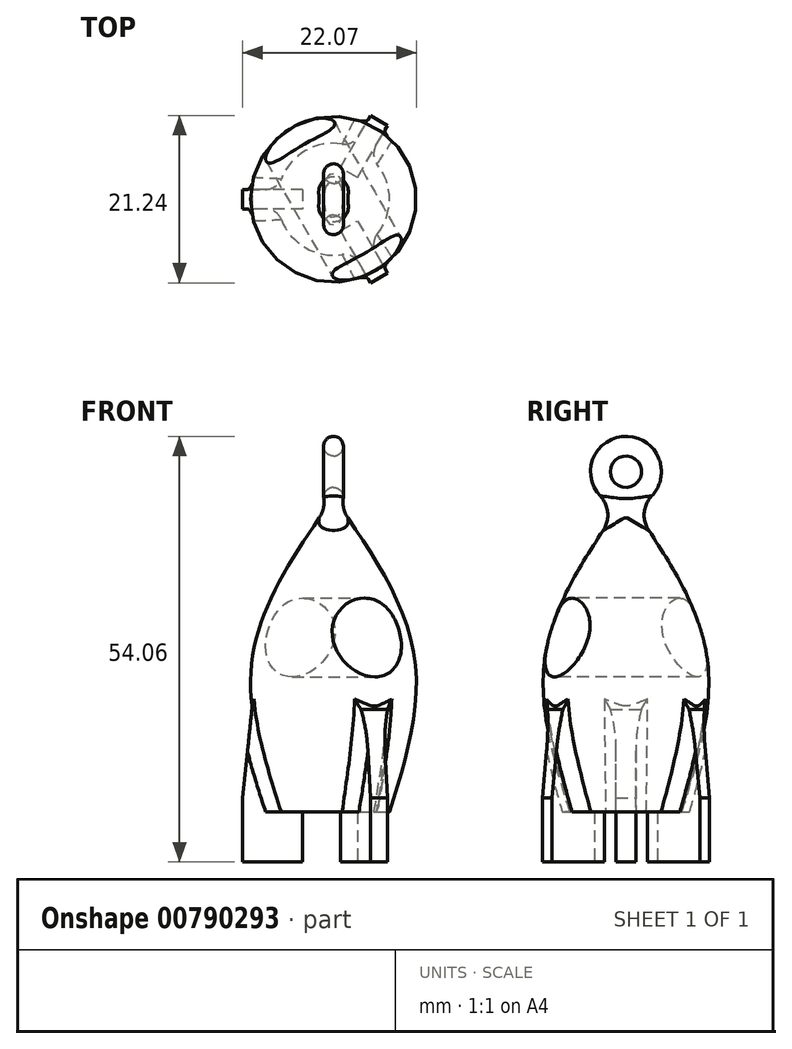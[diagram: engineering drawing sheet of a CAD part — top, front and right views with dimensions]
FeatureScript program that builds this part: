
annotation { "Feature Type Name" : "Feature", "Feature Type Description" : "" }
export const myFeature = defineFeature(function(context is Context, id is Id, definition is map)
    precondition{}
    {
        {
            var Q0;
            Q0=qCreatedBy(makeId("Front.planeOp"),FACE);
            var sketch = newSketch(context, id + "F0", { "sketchPlane" : qUnion([Q0])});
            skLineSegment(sketch, "E0", {"start": v(0, 20) * mm, "end": v(0, -20) * mm});
            skFitSpline(sketch, "E1", {"points": [v(0, 20) * mm, v(-10.25, 0) * mm, v(-7.11, -20) * mm], "startDerivative": vector(-26.7, -38.64) * mm, "endDerivative": vector(12.86, -41.38) * mm});
            skLineSegment(sketch, "E2", {"start": v(-7.11, -20) * mm, "end": v(0, -20) * mm});
            skSolve(sketch);
        }
        {
            var Q0;
            Q0=makeQuery(id+"F0.imprint","IMPRINT",FACE,{"disambiguationData":[TD([[makeQuery(id+"F0.imprint","IMPRINT",EDGE,{"derivedFrom":sQuery(id+"F0.wireOp",EDGE,"E0")}),-1.0]])]});
            var Q1;
            Q1=sQuery(id+"F0.wireOp",EDGE,"E0");
            revolve(context, id + "F1", {"surfaceOperationType" : NewSurfaceOperationType.NEW, "entities" : qUnion([Q0]), "axis" : qUnion([Q1]), "revolveType" : RevolveType.FULL});
        }
        {
            var Q0;
            Q0=qCreatedBy(makeId("Front.planeOp"),FACE);
            var sketch = newSketch(context, id + "F2", { "sketchPlane" : qUnion([Q0])});
            skLineSegment(sketch, "E3", {"start": v(-3.9, -6.95) * mm, "end": v(-3.9, -26.33) * mm});
            skLineSegment(sketch, "E4", {"start": v(-3.9, -26.33) * mm, "end": v(-11.54, -26.33) * mm});
            skLineSegment(sketch, "E5", {"start": v(-11.54, -26.33) * mm, "end": v(-11.54, -18.2) * mm});
            skLineSegment(sketch, "E6", {"start": v(-11.54, -18.2) * mm, "end": v(-10.37, -6.95) * mm});
            skLineSegment(sketch, "E7", {"start": v(-10.37, -6.95) * mm, "end": v(-3.9, -6.95) * mm});
            skSolve(sketch);
        }
        {
            var Q0;
            Q0 = qSketchRegion(id + "F2", true);
            extrude(context, id + "F3", {"entities" : qUnion([Q0]), "depth" : 2.5 * mm, "offsetDistance" : 25 * mm, "symmetric" : true});
        }
        {
            var Q0;
            Q0=makeQuery(id+"F3.opExtrude","SWEPT_BODY",BODY,{"disambiguationData":[OSD([sQuery(id+"F2.wireOp",EDGE,"E3"),sQuery(id+"F2.wireOp",EDGE,"E4"),sQuery(id+"F2.wireOp",EDGE,"E5"),sQuery(id+"F2.wireOp",EDGE,"E6"),sQuery(id+"F2.wireOp",EDGE,"E7")])]});
            var Q1;
            Q1=sQuery(id+"F0.wireOp",EDGE,"E0");
            circularPattern(context, id + "F4", {"entities" : qUnion([Q0]), "axis" : qUnion([Q1]), "angle" : 360 * degree, "instanceCount" : 3, "equalSpace" : true});
        }
        {
            var Q0;
            Q0=makeQuery(id+"F4.opPattern","COPY",FACE,{"derivedFrom":makeQuery(id+"F3.opExtrude","SWEPT_FACE",FACE,{"disambiguationData":[OSD([sQuery(id+"F2.wireOp",EDGE,"E5")])]}),"instanceName":"2"});
            var sketch = newSketch(context, id + "F5", { "sketchPlane" : qUnion([Q0])});
            skCircle(sketch, "E8", {"center": v(0, 2.17) * mm, "radius": 5 * mm});
            skSolve(sketch);
        }
        {
            var Q0;
            Q0=makeQuery(id+"F5.imprint","IMPRINT",FACE,{"disambiguationData":[TD([[makeQuery(id+"F5.imprint","IMPRINT",EDGE,{"derivedFrom":sQuery(id+"F5.wireOp",EDGE,"E8")}),1.0]])]});
            extrude(context, id + "F6", {"entities" : qUnion([Q0]), "operationType" : NewBodyOperationType.REMOVE, "endBound" : BoundingType.THROUGH_ALL, "oppositeDirection" : true, "depth" : 25 * mm, "offsetDistance" : 25 * mm});
        }
        {
            var Q0;
            Q0=qCreatedBy(makeId("Front.planeOp"),FACE);
            var sketch = newSketch(context, id + "F7", { "sketchPlane" : qUnion([Q0])});
            skCircle(sketch, "E9", {"center": v(0, 19.98) * mm, "radius": 1.25 * mm});
            skLineSegment(sketch, "E10", {"start": v(-4.69, 23.23) * mm, "end": v(7.72, 23.23) * mm});
            skSolve(sketch);
        }
        {
            var Q0;
            Q0 = qSketchRegion(id + "F7", true);
            var Q1;
            Q1=sQuery(id+"F7.wireOp",EDGE,"E10");
            revolve(context, id + "F8", {"surfaceOperationType" : NewSurfaceOperationType.NEW, "entities" : qUnion([Q0]), "axis" : qUnion([Q1]), "revolveType" : RevolveType.FULL});
        }
        {
            var Q0;
            Q0=makeQuery(id+"F1.opRevolve","SWEPT_BODY",BODY,{"disambiguationData":[OSD([sQuery(id+"F0.wireOp",EDGE,"E0"),sQuery(id+"F0.wireOp",EDGE,"E1"),sQuery(id+"F0.wireOp",EDGE,"E2")])]});
            var Q1;
            Q1=makeQuery(id+"F3.opExtrude","SWEPT_BODY",BODY,{"disambiguationData":[OSD([sQuery(id+"F2.wireOp",EDGE,"E3"),sQuery(id+"F2.wireOp",EDGE,"E4"),sQuery(id+"F2.wireOp",EDGE,"E5"),sQuery(id+"F2.wireOp",EDGE,"E6"),sQuery(id+"F2.wireOp",EDGE,"E7")])]});
            var Q2;
            Q2=makeQuery(id+"F4.opPattern","COPY",BODY,{"derivedFrom":makeQuery(id+"F3.opExtrude","SWEPT_BODY",BODY,{"disambiguationData":[OSD([sQuery(id+"F2.wireOp",EDGE,"E3"),sQuery(id+"F2.wireOp",EDGE,"E4"),sQuery(id+"F2.wireOp",EDGE,"E5"),sQuery(id+"F2.wireOp",EDGE,"E6"),sQuery(id+"F2.wireOp",EDGE,"E7")])]}),"instanceName":"1"});
            var Q3;
            Q3=makeQuery(id+"F4.opPattern","COPY",BODY,{"derivedFrom":makeQuery(id+"F3.opExtrude","SWEPT_BODY",BODY,{"disambiguationData":[OSD([sQuery(id+"F2.wireOp",EDGE,"E3"),sQuery(id+"F2.wireOp",EDGE,"E4"),sQuery(id+"F2.wireOp",EDGE,"E5"),sQuery(id+"F2.wireOp",EDGE,"E6"),sQuery(id+"F2.wireOp",EDGE,"E7")])]}),"instanceName":"2"});
            var Q4;
            Q4=makeQuery(id+"F8.opRevolve","SWEPT_BODY",BODY,{"disambiguationData":[OSD([sQuery(id+"F7.wireOp",EDGE,"E9")])]});
            booleanBodies(context, id + "F9", {"operationType" : BooleanOperationType.UNION, "tools" : qUnion([Q0, Q1, Q2, Q3, Q4])});
        }
        {
            var Q0;
            Q0=makeQuery(id+"F9.opBoolean","INTERSECT",EDGE,{"derivedFrom":[makeQuery(id+"F1.opRevolve","SWEPT_FACE",FACE,{"disambiguationData":[OSD([sQuery(id+"F0.wireOp",EDGE,"E1")])]}),makeQuery(id+"F8.opRevolve","SWEPT_FACE",FACE,{"disambiguationData":[OSD([sQuery(id+"F7.wireOp",EDGE,"E9")])]})]});
            fillet(context, id + "F10", {"entities" : qUnion([Q0]), "radius" : 3.5 * mm, "tangentPropagation" : true, "allowEdgeOverflow" : false});
        }
        {
            var Q0;
            Q0=makeQuery(id+"F9.opBoolean","INTERSECT",EDGE,{"derivedFrom":[makeQuery(id+"F4.opPattern","COPY",FACE,{"derivedFrom":makeQuery(id+"F3.opExtrude","CAP_FACE",FACE,{"disambiguationData":[OSD([sQuery(id+"F2.wireOp",EDGE,"E3"),sQuery(id+"F2.wireOp",EDGE,"E4"),sQuery(id+"F2.wireOp",EDGE,"E5"),sQuery(id+"F2.wireOp",EDGE,"E6"),sQuery(id+"F2.wireOp",EDGE,"E7")])],"isStart":false}),"instanceName":"1"}),makeQuery(id+"F1.opRevolve","SWEPT_FACE",FACE,{"disambiguationData":[OSD([sQuery(id+"F0.wireOp",EDGE,"E1")])]})]});
            var Q1;
            Q1=makeQuery(id+"F9.opBoolean","INTERSECT",EDGE,{"derivedFrom":[makeQuery(id+"F4.opPattern","COPY",FACE,{"derivedFrom":makeQuery(id+"F3.opExtrude","CAP_FACE",FACE,{"disambiguationData":[OSD([sQuery(id+"F2.wireOp",EDGE,"E3"),sQuery(id+"F2.wireOp",EDGE,"E4"),sQuery(id+"F2.wireOp",EDGE,"E5"),sQuery(id+"F2.wireOp",EDGE,"E6"),sQuery(id+"F2.wireOp",EDGE,"E7")])],"isStart":true}),"instanceName":"1"}),makeQuery(id+"F1.opRevolve","SWEPT_FACE",FACE,{"disambiguationData":[OSD([sQuery(id+"F0.wireOp",EDGE,"E1")])]})]});
            fillet(context, id + "F11", {"entities" : qUnion([Q0, Q1]), "radius" : 2 * mm, "tangentPropagation" : true, "allowEdgeOverflow" : false});
        }
        {
            var Q0;
            Q0=makeQuery(id+"F9.opBoolean","INTERSECT",EDGE,{"derivedFrom":[makeQuery(id+"F4.opPattern","COPY",FACE,{"derivedFrom":makeQuery(id+"F3.opExtrude","CAP_FACE",FACE,{"disambiguationData":[OSD([sQuery(id+"F2.wireOp",EDGE,"E3"),sQuery(id+"F2.wireOp",EDGE,"E4"),sQuery(id+"F2.wireOp",EDGE,"E5"),sQuery(id+"F2.wireOp",EDGE,"E6"),sQuery(id+"F2.wireOp",EDGE,"E7")])],"isStart":false}),"instanceName":"2"}),makeQuery(id+"F1.opRevolve","SWEPT_FACE",FACE,{"disambiguationData":[OSD([sQuery(id+"F0.wireOp",EDGE,"E1")])]})]});
            var Q1;
            Q1=makeQuery(id+"F9.opBoolean","INTERSECT",EDGE,{"derivedFrom":[makeQuery(id+"F4.opPattern","COPY",FACE,{"derivedFrom":makeQuery(id+"F3.opExtrude","CAP_FACE",FACE,{"disambiguationData":[OSD([sQuery(id+"F2.wireOp",EDGE,"E3"),sQuery(id+"F2.wireOp",EDGE,"E4"),sQuery(id+"F2.wireOp",EDGE,"E5"),sQuery(id+"F2.wireOp",EDGE,"E6"),sQuery(id+"F2.wireOp",EDGE,"E7")])],"isStart":true}),"instanceName":"2"}),makeQuery(id+"F1.opRevolve","SWEPT_FACE",FACE,{"disambiguationData":[OSD([sQuery(id+"F0.wireOp",EDGE,"E1")])]})]});
            fillet(context, id + "F12", {"entities" : qUnion([Q0, Q1]), "radius" : 2 * mm, "tangentPropagation" : true, "allowEdgeOverflow" : false});
        }
        {
            var Q0;
            Q0=makeQuery(id+"F9.opBoolean","INTERSECT",EDGE,{"derivedFrom":[makeQuery(id+"F3.opExtrude","CAP_FACE",FACE,{"disambiguationData":[OSD([sQuery(id+"F2.wireOp",EDGE,"E3"),sQuery(id+"F2.wireOp",EDGE,"E4"),sQuery(id+"F2.wireOp",EDGE,"E5"),sQuery(id+"F2.wireOp",EDGE,"E6"),sQuery(id+"F2.wireOp",EDGE,"E7")])],"isStart":true}),makeQuery(id+"F1.opRevolve","SWEPT_FACE",FACE,{"disambiguationData":[OSD([sQuery(id+"F0.wireOp",EDGE,"E1")])]})]});
            var Q1;
            Q1=makeQuery(id+"F9.opBoolean","INTERSECT",EDGE,{"derivedFrom":[makeQuery(id+"F3.opExtrude","CAP_FACE",FACE,{"disambiguationData":[OSD([sQuery(id+"F2.wireOp",EDGE,"E3"),sQuery(id+"F2.wireOp",EDGE,"E4"),sQuery(id+"F2.wireOp",EDGE,"E5"),sQuery(id+"F2.wireOp",EDGE,"E6"),sQuery(id+"F2.wireOp",EDGE,"E7")])],"isStart":false}),makeQuery(id+"F1.opRevolve","SWEPT_FACE",FACE,{"disambiguationData":[OSD([sQuery(id+"F0.wireOp",EDGE,"E1")])]})]});
            fillet(context, id + "F13", {"entities" : qUnion([Q0, Q1]), "radius" : 2 * mm, "tangentPropagation" : true, "allowEdgeOverflow" : false});
        }
        {
            var Q0;
            Q0=makeQuery(id+"F9.opBoolean","INTERSECT",EDGE,{"derivedFrom":[makeQuery(id+"F4.opPattern","COPY",FACE,{"derivedFrom":makeQuery(id+"F3.opExtrude","SWEPT_FACE",FACE,{"disambiguationData":[OSD([sQuery(id+"F2.wireOp",EDGE,"E7")])]}),"instanceName":"2"}),makeQuery(id+"F1.opRevolve","SWEPT_FACE",FACE,{"disambiguationData":[OSD([sQuery(id+"F0.wireOp",EDGE,"E1")])]})]});
            fillet(context, id + "F14", {"entities" : qUnion([Q0]), "radius" : 2 * mm, "tangentPropagation" : true, "allowEdgeOverflow" : false});
        }
        {
            var Q0;
            Q0=makeQuery(id+"F9.opBoolean","INTERSECT",EDGE,{"derivedFrom":[makeQuery(id+"F4.opPattern","COPY",FACE,{"derivedFrom":makeQuery(id+"F3.opExtrude","SWEPT_FACE",FACE,{"disambiguationData":[OSD([sQuery(id+"F2.wireOp",EDGE,"E7")])]}),"instanceName":"1"}),makeQuery(id+"F1.opRevolve","SWEPT_FACE",FACE,{"disambiguationData":[OSD([sQuery(id+"F0.wireOp",EDGE,"E1")])]})]});
            fillet(context, id + "F15", {"entities" : qUnion([Q0]), "radius" : 2 * mm, "tangentPropagation" : true, "allowEdgeOverflow" : false});
        }
        {
            var Q0;
            Q0=makeQuery(id+"F9.opBoolean","INTERSECT",EDGE,{"derivedFrom":[makeQuery(id+"F3.opExtrude","SWEPT_FACE",FACE,{"disambiguationData":[OSD([sQuery(id+"F2.wireOp",EDGE,"E7")])]}),makeQuery(id+"F1.opRevolve","SWEPT_FACE",FACE,{"disambiguationData":[OSD([sQuery(id+"F0.wireOp",EDGE,"E1")])]})]});
            fillet(context, id + "F16", {"entities" : qUnion([Q0]), "radius" : 2 * mm, "tangentPropagation" : true, "allowEdgeOverflow" : false});
        }
    });
